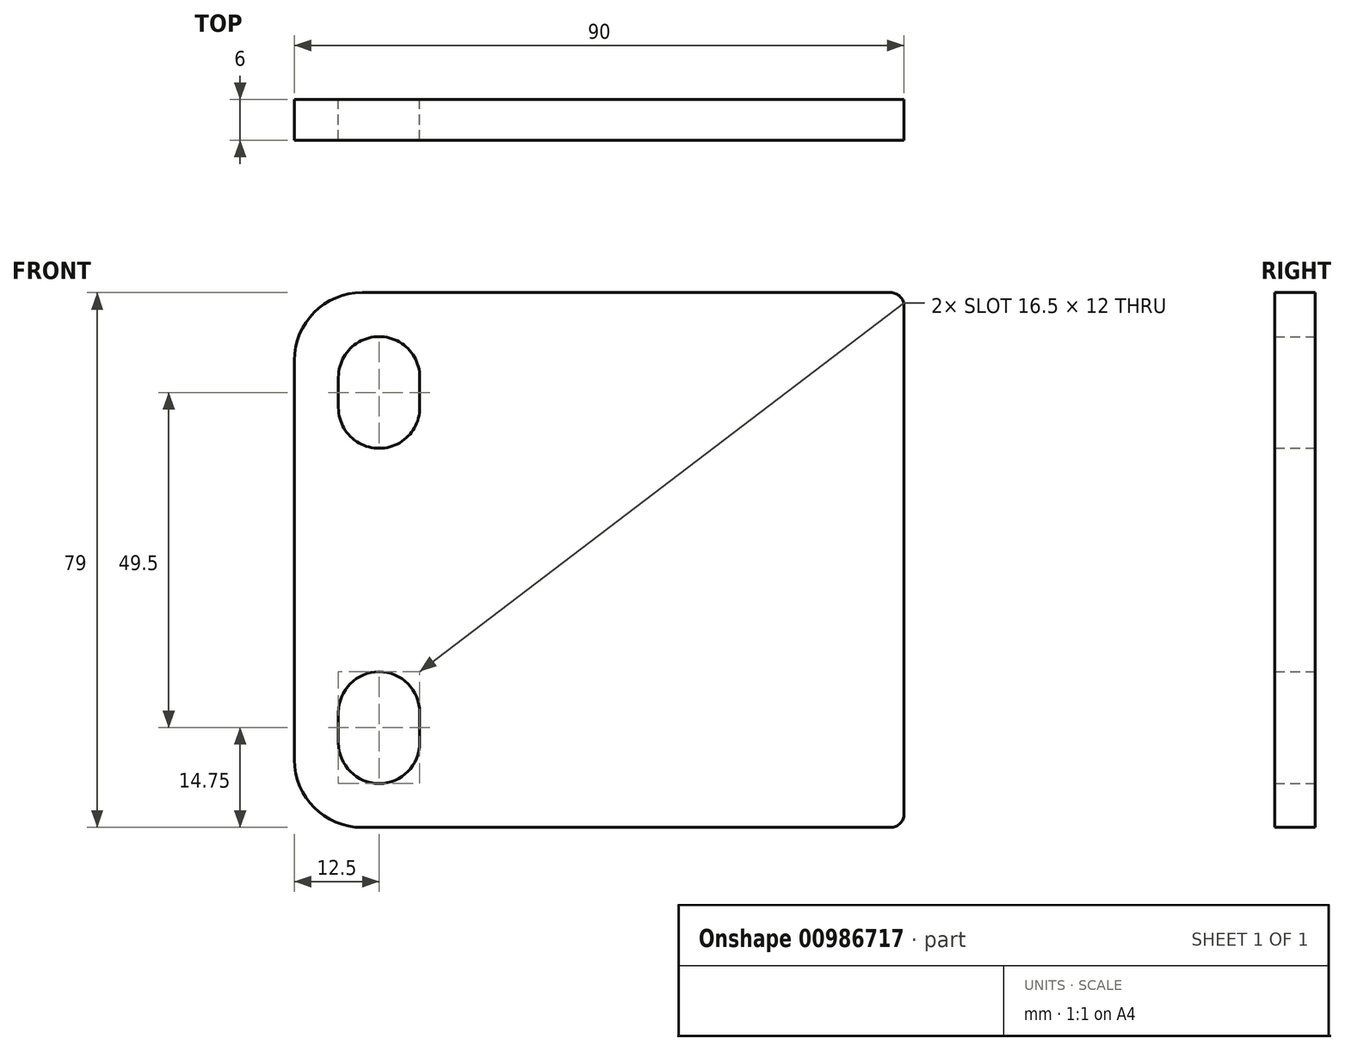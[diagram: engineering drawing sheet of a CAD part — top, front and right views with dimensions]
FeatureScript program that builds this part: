
annotation { "Feature Type Name" : "Feature", "Feature Type Description" : "" }
export const myFeature = defineFeature(function(context is Context, id is Id, definition is map)
    precondition{}
    {
        {
            var Q0;
            Q0=qCreatedBy(makeId("Front.planeOp"),FACE);
            var sketch = newSketch(context, id + "F0", { "sketchPlane" : qUnion([Q0])});
            skLineSegment(sketch, "E0.bottom", {"start": v(-35, -39.5) * mm, "end": v(43, -39.5) * mm});
            skLineSegment(sketch, "E0.top", {"start": v(-35, 39.5) * mm, "end": v(43, 39.5) * mm});
            skLineSegment(sketch, "E0.left", {"start": v(-45, -29.5) * mm, "end": v(-45, 29.5) * mm});
            skLineSegment(sketch, "E0.right", {"start": v(45, -37.5) * mm, "end": v(45, 37.5) * mm});
            skPoint(sketch, "E0.middle", {"position": v(0, 0) * mm});
            skLineSegment(sketch, "E1", {"start": v(-45, 39.5) * mm, "end": v(-45, 22.5) * mm, "construction": true});
            skLineSegment(sketch, "E2", {"start": v(-45, 22.5) * mm, "end": v(-32.5, 22.5) * mm, "construction": true});
            skLineSegment(sketch, "E3", {"start": v(-32.5, 22.5) * mm, "end": v(-32.5, -22.5) * mm, "construction": true});
            skArc(sketch, "E4", {"start": v(-38.5, 22.5) * mm, "mid": v(-32.47, 16.5) * mm, "end": v(-26.5, 22.56) * mm});
            skArc(sketch, "E5", {"start": v(-26.5, -22.5) * mm, "mid": v(-32.5, -16.5) * mm, "end": v(-38.5, -22.5) * mm});
            skPoint(sketch, "E6.visualSharp", {"position": v(-45, 39.5) * mm});
            skArc(sketch, "E6.filletArc", {"start": v(-35, 39.5) * mm, "mid": v(-42.07, 36.57) * mm, "end": v(-45, 29.5) * mm});
            skPoint(sketch, "E7.visualSharp", {"position": v(-45, -39.5) * mm});
            skArc(sketch, "E7.filletArc", {"start": v(-45, -29.5) * mm, "mid": v(-42.07, -36.57) * mm, "end": v(-35, -39.5) * mm});
            skPoint(sketch, "E8.visualSharp", {"position": v(45, 39.5) * mm});
            skArc(sketch, "E8.filletArc", {"start": v(45, 37.5) * mm, "mid": v(44.41, 38.91) * mm, "end": v(43, 39.5) * mm});
            skPoint(sketch, "E9.visualSharp", {"position": v(45, -39.5) * mm});
            skArc(sketch, "E9.filletArc", {"start": v(43, -39.5) * mm, "mid": v(44.41, -38.91) * mm, "end": v(45, -37.5) * mm});
            skLineSegment(sketch, "E10", {"start": v(-32.5, 22.5) * mm, "end": v(-32.5, 27) * mm, "construction": true});
            skLineSegment(sketch, "E11", {"start": v(-32.5, -22.5) * mm, "end": v(-32.5, -27) * mm, "construction": true});
            skArc(sketch, "E12", {"start": v(-38.5, -27) * mm, "mid": v(-32.5, -33) * mm, "end": v(-26.5, -27) * mm});
            skLineSegment(sketch, "E13", {"start": v(-26.5, 22.44) * mm, "end": v(-26.5, 27) * mm});
            skLineSegment(sketch, "E14", {"start": v(-38.5, 22.5) * mm, "end": v(-38.5, 27) * mm});
            skArc(sketch, "E15.trimOffspring", {"start": v(-26.5, 27) * mm, "mid": v(-32.5, 33) * mm, "end": v(-38.5, 27) * mm});
            skLineSegment(sketch, "E16", {"start": v(-26.5, -22.5) * mm, "end": v(-26.5, -27) * mm});
            skLineSegment(sketch, "E17.0", {"start": v(-38.5, -22.5) * mm, "end": v(-38.5, -27) * mm});
            skSolve(sketch);
        }
        {
            var Q0;
            Q0=makeQuery(id+"F0.imprint","IMPRINT",FACE,{"disambiguationData":[TD([[makeQuery(id+"F0.imprint","IMPRINT",EDGE,{"derivedFrom":sQuery(id+"F0.wireOp",EDGE,"E0.bottom")}),1.0]])]});
            extrude(context, id + "F1", {"entities" : qUnion([Q0]), "depth" : 6 * mm, "offsetDistance" : 25 * mm});
        }
    });
